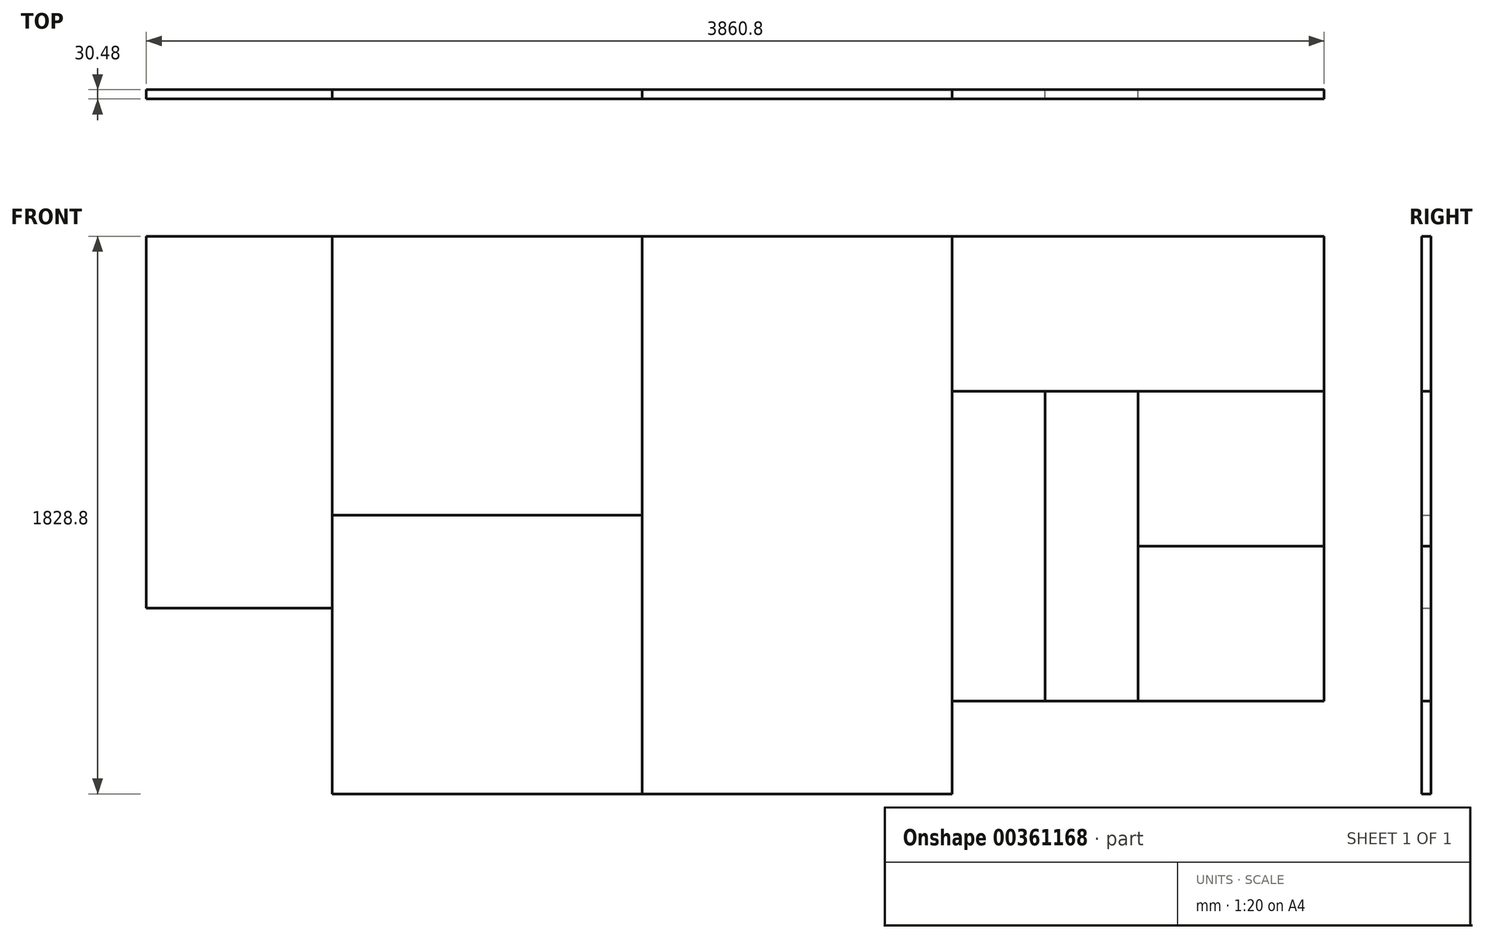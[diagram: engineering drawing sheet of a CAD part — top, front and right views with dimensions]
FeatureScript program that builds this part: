
annotation { "Feature Type Name" : "Feature", "Feature Type Description" : "" }
export const myFeature = defineFeature(function(context is Context, id is Id, definition is map)
    precondition{}
    {
        {
            var Q0;
            Q0=qCreatedBy(makeId("Front.planeOp"),FACE);
            var sketch = newSketch(context, id + "F0", { "sketchPlane" : qUnion([Q0])});
            skLineSegment(sketch, "E0.bottom", {"start": v(0, 0) * mm, "end": v(609.6, 0) * mm});
            skLineSegment(sketch, "E0.top", {"start": v(0, -1219.2) * mm, "end": v(609.6, -1219.2) * mm});
            skLineSegment(sketch, "E0.left", {"start": v(0, 0) * mm, "end": v(0, -1219.2) * mm});
            skLineSegment(sketch, "E0.right", {"start": v(609.6, 0) * mm, "end": v(609.6, -1219.2) * mm});
            skLineSegment(sketch, "E1.bottom", {"start": v(609.6, 0) * mm, "end": v(1625.6, 0) * mm});
            skLineSegment(sketch, "E1.top", {"start": v(609.6, -914.4) * mm, "end": v(1625.6, -914.4) * mm});
            skLineSegment(sketch, "E1.left", {"start": v(609.6, 0) * mm, "end": v(609.6, -914.4) * mm});
            skLineSegment(sketch, "E1.right", {"start": v(1625.6, 0) * mm, "end": v(1625.6, -914.4) * mm});
            skLineSegment(sketch, "E2.top", {"start": v(609.6, -1828.8) * mm, "end": v(1625.6, -1828.8) * mm});
            skLineSegment(sketch, "E2.left", {"start": v(609.6, -914.4) * mm, "end": v(609.6, -1828.8) * mm});
            skLineSegment(sketch, "E2.right", {"start": v(1625.6, -914.4) * mm, "end": v(1625.6, -1828.8) * mm});
            skLineSegment(sketch, "E3.bottom", {"start": v(1625.6, 0) * mm, "end": v(2641.6, 0) * mm});
            skLineSegment(sketch, "E3.top", {"start": v(1625.6, -1828.8) * mm, "end": v(2641.6, -1828.8) * mm});
            skLineSegment(sketch, "E3.left", {"start": v(1625.6, 0) * mm, "end": v(1625.6, -1828.8) * mm});
            skLineSegment(sketch, "E3.right", {"start": v(2641.6, 0) * mm, "end": v(2641.6, -1828.8) * mm});
            skLineSegment(sketch, "E4.bottom", {"start": v(2641.6, 0) * mm, "end": v(3860.8, 0) * mm});
            skLineSegment(sketch, "E4.top", {"start": v(2641.6, -508) * mm, "end": v(3860.8, -508) * mm});
            skLineSegment(sketch, "E4.left", {"start": v(2641.6, 0) * mm, "end": v(2641.6, -508) * mm});
            skLineSegment(sketch, "E4.right", {"start": v(3860.8, 0) * mm, "end": v(3860.8, -508) * mm});
            skLineSegment(sketch, "E5.bottom", {"start": v(2641.6, -508) * mm, "end": v(2946.4, -508) * mm});
            skLineSegment(sketch, "E5.top", {"start": v(2641.6, -1524) * mm, "end": v(2946.4, -1524) * mm});
            skLineSegment(sketch, "E5.left", {"start": v(2641.6, -508) * mm, "end": v(2641.6, -1524) * mm});
            skLineSegment(sketch, "E5.right", {"start": v(2946.4, -508) * mm, "end": v(2946.4, -1524) * mm});
            skLineSegment(sketch, "E6.bottom", {"start": v(2946.4, -508) * mm, "end": v(3251.2, -508) * mm});
            skLineSegment(sketch, "E6.top", {"start": v(2946.4, -1524) * mm, "end": v(3251.2, -1524) * mm});
            skLineSegment(sketch, "E6.right", {"start": v(3251.2, -508) * mm, "end": v(3251.2, -1524) * mm});
            skLineSegment(sketch, "E7.bottom", {"start": v(3251.2, -508) * mm, "end": v(3860.8, -508) * mm});
            skLineSegment(sketch, "E7.top", {"start": v(3251.2, -1016) * mm, "end": v(3860.8, -1016) * mm});
            skLineSegment(sketch, "E7.left", {"start": v(3251.2, -508) * mm, "end": v(3251.2, -1016) * mm});
            skLineSegment(sketch, "E7.right", {"start": v(3860.8, -508) * mm, "end": v(3860.8, -1016) * mm});
            skLineSegment(sketch, "E8.top", {"start": v(3251.2, -1524) * mm, "end": v(3860.8, -1524) * mm});
            skLineSegment(sketch, "E8.left", {"start": v(3251.2, -1016) * mm, "end": v(3251.2, -1524) * mm});
            skLineSegment(sketch, "E8.right", {"start": v(3860.8, -1016) * mm, "end": v(3860.8, -1524) * mm});
            skSolve(sketch);
        }
        {
            var Q0;
            {var subQ1=sQuery(id+"F0.wireOp",EDGE,"E0.bottom");Q0=makeQuery(id+"F0.imprint","IMPRINT",FACE,{"disambiguationData":[TD([[makeQuery(id+"F0.imprint","IMPRINT",EDGE,{"derivedFrom":subQ1}),-1.0]])]});}
            var Q1;
            Q1=makeQuery(id+"F0.imprint","IMPRINT",FACE,{"disambiguationData":[TD([[makeQuery(id+"F0.imprint","IMPRINT",EDGE,{"derivedFrom":sQuery(id+"F0.wireOp",EDGE,"E1.right")}),1.0]])]});
            var Q2;
            {var subQ3=sQuery(id+"F0.wireOp",EDGE,"E5.right");Q2=makeQuery(id+"F0.imprint","IMPRINT",FACE,{"disambiguationData":[TD([[makeQuery(id+"F0.imprint","IMPRINT",EDGE,{"derivedFrom":subQ3}),1.0]])]});}
            extrude(context, id + "F1", {"entities" : qUnion([Q0, Q1, Q2]), "depth" : 30.48 * mm, "offsetDistance" : 30.48 * mm});
        }
        {
            var Q0;
            {var subQ0=sQuery(id+"F0.wireOp",EDGE,"E1.bottom");Q0=makeQuery(id+"F0.imprint","IMPRINT",FACE,{"disambiguationData":[TD([[makeQuery(id+"F0.imprint","IMPRINT",EDGE,{"derivedFrom":subQ0}),-1.0]])]});}
            var Q1;
            {var subQ4=sQuery(id+"F0.wireOp",EDGE,"E4.bottom");Q1=makeQuery(id+"F0.imprint","IMPRINT",FACE,{"disambiguationData":[TD([[makeQuery(id+"F0.imprint","IMPRINT",EDGE,{"derivedFrom":subQ4}),-1.0]])]});}
            var Q2;
            {var subQ2=sQuery(id+"F0.wireOp",EDGE,"E7.top");Q2=makeQuery(id+"F0.imprint","IMPRINT",FACE,{"disambiguationData":[TD([[makeQuery(id+"F0.imprint","IMPRINT",EDGE,{"derivedFrom":subQ2}),-1.0]])]});}
            extrude(context, id + "F2", {"entities" : qUnion([Q0, Q1, Q2]), "depth" : 30.48 * mm, "offsetDistance" : 30.48 * mm});
        }
        {
            var Q0;
            {var subQ0=sQuery(id+"F0.wireOp",EDGE,"E1.top");Q0=makeQuery(id+"F0.imprint","IMPRINT",FACE,{"disambiguationData":[TD([[makeQuery(id+"F0.imprint","IMPRINT",EDGE,{"derivedFrom":subQ0}),-1.0]])]});}
            var Q1;
            {var subQ3=sQuery(id+"F0.wireOp",EDGE,"E5.top");Q1=makeQuery(id+"F0.imprint","IMPRINT",FACE,{"disambiguationData":[TD([[makeQuery(id+"F0.imprint","IMPRINT",EDGE,{"derivedFrom":subQ3}),1.0]])]});}
            var Q2;
            {var subQ4=sQuery(id+"F0.wireOp",EDGE,"E7.top");Q2=makeQuery(id+"F0.imprint","IMPRINT",FACE,{"disambiguationData":[TD([[makeQuery(id+"F0.imprint","IMPRINT",EDGE,{"derivedFrom":subQ4}),1.0]])]});}
            extrude(context, id + "F3", {"entities" : qUnion([Q0, Q1, Q2]), "depth" : 30.48 * mm, "offsetDistance" : 30.48 * mm});
        }
    });
